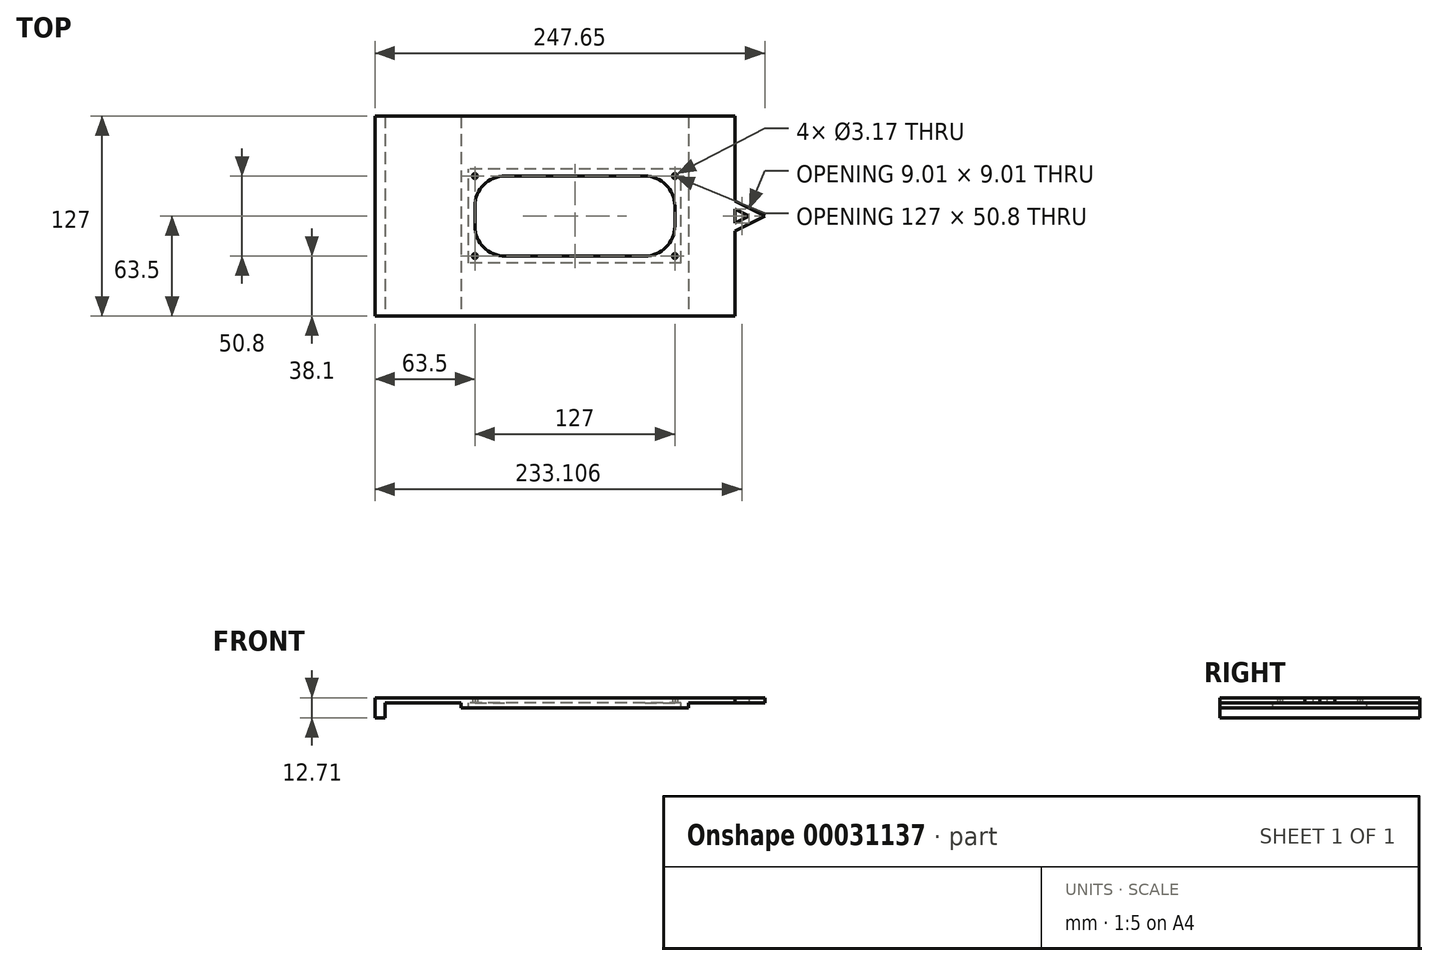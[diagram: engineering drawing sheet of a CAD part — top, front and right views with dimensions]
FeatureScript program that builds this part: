
annotation { "Feature Type Name" : "Feature", "Feature Type Description" : "" }
export const myFeature = defineFeature(function(context is Context, id is Id, definition is map)
    precondition{}
    {
        {
            var Q0;
            Q0=qCreatedBy(makeId("Top.planeOp"),FACE);
            var sketch = newSketch(context, id + "F0", { "sketchPlane" : qUnion([Q0])});
            skLineSegment(sketch, "E0.rect.left", {"start": v(101.6, -63.5) * mm, "end": v(101.6, -9.53) * mm});
            skPoint(sketch, "E0.rect.middle", {"position": v(0, 0) * mm});
            skLineSegment(sketch, "E1.rect.right", {"start": v(-127, -63.5) * mm, "end": v(-127, 63.5) * mm});
            skLineSegment(sketch, "E2.rect.bottom", {"start": v(-127, -63.5) * mm, "end": v(101.6, -63.5) * mm});
            skLineSegment(sketch, "E2.rect.top", {"start": v(-127, 63.5) * mm, "end": v(101.6, 63.5) * mm});
            skLineSegment(sketch, "E3.rect.bottom", {"start": v(44.45, -25.4) * mm, "end": v(-44.45, -25.4) * mm});
            skLineSegment(sketch, "E3.rect.top", {"start": v(44.45, 25.4) * mm, "end": v(-44.45, 25.4) * mm});
            skLineSegment(sketch, "E3.rect.left", {"start": v(63.5, -6.35) * mm, "end": v(63.5, 6.35) * mm});
            skLineSegment(sketch, "E3.rect.right", {"start": v(-63.5, -6.35) * mm, "end": v(-63.5, 6.35) * mm});
            skPoint(sketch, "E4.visualSharp", {"position": v(-63.5, 25.4) * mm});
            skArc(sketch, "E4.filletArc", {"start": v(-44.45, 25.4) * mm, "mid": v(-57.92, 19.82) * mm, "end": v(-63.5, 6.35) * mm});
            skPoint(sketch, "E5.visualSharp", {"position": v(-63.5, -25.4) * mm});
            skArc(sketch, "E5.filletArc", {"start": v(-63.5, -6.35) * mm, "mid": v(-57.92, -19.82) * mm, "end": v(-44.45, -25.4) * mm});
            skPoint(sketch, "E6.visualSharp", {"position": v(63.5, -25.4) * mm});
            skArc(sketch, "E6.filletArc", {"start": v(44.45, -25.4) * mm, "mid": v(57.92, -19.82) * mm, "end": v(63.5, -6.35) * mm});
            skPoint(sketch, "E7.visualSharp", {"position": v(63.5, 25.4) * mm});
            skArc(sketch, "E7.filletArc", {"start": v(63.5, 6.35) * mm, "mid": v(57.92, 19.82) * mm, "end": v(44.45, 25.4) * mm});
            skPoint(sketch, "E8.orphan", {"position": v(-127, 92.44) * mm});
            skPoint(sketch, "E0.rect.top.end.orphan", {"position": v(-101.6, 76.2) * mm});
            skPoint(sketch, "E9.orphan", {"position": v(101.6, 76.2) * mm});
            skPoint(sketch, "E10.orphan", {"position": v(127, 92.44) * mm});
            skPoint(sketch, "E11.orphan", {"position": v(133.35, 63.5) * mm});
            skPoint(sketch, "E12.trimOffspring.end.orphan", {"position": v(133.35, -63.5) * mm});
            skPoint(sketch, "E1.rect.bottom.start.orphan", {"position": v(127, -92.44) * mm});
            skPoint(sketch, "E13.orphan", {"position": v(-101.6, -76.2) * mm});
            skPoint(sketch, "E14.orphan", {"position": v(101.6, -76.2) * mm});
            skPoint(sketch, "E15.orphan", {"position": v(-127, -92.44) * mm});
            skCircle(sketch, "E16", {"center": v(-63.5, -25.4) * mm, "radius": 1.59 * mm});
            skCircle(sketch, "E17", {"center": v(-63.5, 25.4) * mm, "radius": 1.59 * mm});
            skCircle(sketch, "E18", {"center": v(63.5, 25.4) * mm, "radius": 1.59 * mm});
            skCircle(sketch, "E19", {"center": v(63.5, -25.4) * mm, "radius": 1.59 * mm});
            skLineSegment(sketch, "E20.rect.bottom", {"start": v(67.52, -29.8) * mm, "end": v(-67.52, -29.8) * mm});
            skLineSegment(sketch, "E20.rect.top", {"start": v(67.52, 29.8) * mm, "end": v(-67.52, 29.8) * mm});
            skLineSegment(sketch, "E20.rect.left", {"start": v(67.52, -29.8) * mm, "end": v(67.52, 29.8) * mm});
            skLineSegment(sketch, "E20.rect.right", {"start": v(-67.52, -29.8) * mm, "end": v(-67.52, 29.8) * mm});
            skLineSegment(sketch, "E21", {"start": v(-72.28, 34.56) * mm, "end": v(72.28, 34.56) * mm});
            skLineSegment(sketch, "E22", {"start": v(72.28, 34.56) * mm, "end": v(72.28, -34.56) * mm});
            skLineSegment(sketch, "E23", {"start": v(72.28, -34.56) * mm, "end": v(-72.28, -34.56) * mm});
            skLineSegment(sketch, "E24", {"start": v(-72.28, -34.56) * mm, "end": v(-72.28, 34.56) * mm});
            skLineSegment(sketch, "E25", {"start": v(-72.28, -34.56) * mm, "end": v(-72.28, -63.5) * mm});
            skLineSegment(sketch, "E26", {"start": v(72.28, -34.56) * mm, "end": v(72.28, -63.5) * mm});
            skLineSegment(sketch, "E27", {"start": v(-72.28, 34.56) * mm, "end": v(-72.28, 63.5) * mm});
            skLineSegment(sketch, "E28", {"start": v(72.28, 34.56) * mm, "end": v(72.28, 63.5) * mm});
            skPoint(sketch, "E29", {"position": v(101.6, 0) * mm});
            skLineSegment(sketch, "E30", {"start": v(120.65, 0) * mm, "end": v(101.6, 9.53) * mm});
            skLineSegment(sketch, "E31", {"start": v(120.65, 0) * mm, "end": v(101.6, -9.52) * mm});
            skLineSegment(sketch, "E32", {"start": v(101.6, -4.5) * mm, "end": v(110.61, 0) * mm});
            skLineSegment(sketch, "E33", {"start": v(110.61, 0) * mm, "end": v(101.6, 4.5) * mm});
            skLineSegment(sketch, "E34.trimOffspring", {"start": v(101.6, 9.52) * mm, "end": v(101.6, 63.5) * mm});
            skLineSegment(sketch, "E35.trimOffspring", {"start": v(101.6, -4.5) * mm, "end": v(101.6, 4.5) * mm});
            skLineSegment(sketch, "E36", {"start": v(-120.65, 63.5) * mm, "end": v(-120.65, -63.5) * mm});
            skPoint(sketch, "E2.rect.left.end.orphan", {"position": v(-133.35, 63.5) * mm});
            skPoint(sketch, "E37.orphan", {"position": v(-133.35, -63.5) * mm});
            skSolve(sketch);
        }
        {
            var Q0;
            Q0=makeQuery(id+"F0.imprint","IMPRINT",FACE,{"disambiguationData":[TD([[makeQuery(id+"F0.imprint","IMPRINT",EDGE,{"derivedFrom":sQuery(id+"F0.wireOp",EDGE,"E23")}),1.0]])]});
            var Q1;
            Q1=makeQuery(id+"F0.imprint","IMPRINT",FACE,{"disambiguationData":[TD([[makeQuery(id+"F0.imprint","IMPRINT",EDGE,{"derivedFrom":sQuery(id+"F0.wireOp",EDGE,"E3.rect.bottom")}),1.0]])]});
            var Q2;
            Q2=makeQuery(id+"F0.imprint","IMPRINT",FACE,{"disambiguationData":[TD([[makeQuery(id+"F0.imprint","IMPRINT",EDGE,{"derivedFrom":sQuery(id+"F0.wireOp",EDGE,"E20.rect.bottom")}),1.0]])]});
            var Q3;
            Q3=makeQuery(id+"F0.imprint","IMPRINT",FACE,{"disambiguationData":[TD([[makeQuery(id+"F0.imprint","IMPRINT",EDGE,{"derivedFrom":sQuery(id+"F0.wireOp",EDGE,"E21")}),1.0]])]});
            var Q4;
            {var subQ3=sQuery(id+"F0.wireOp",EDGE,"E0.rect.left");Q4=makeQuery(id+"F0.imprint","IMPRINT",FACE,{"disambiguationData":[TD([[makeQuery(id+"F0.imprint","IMPRINT",EDGE,{"derivedFrom":subQ3}),1.0]])]});}
            var Q5;
            {var subQ3=sQuery(id+"F0.wireOp",EDGE,"E1.rect.right");Q5=makeQuery(id+"F0.imprint","IMPRINT",FACE,{"disambiguationData":[TD([[makeQuery(id+"F0.imprint","IMPRINT",EDGE,{"derivedFrom":subQ3}),-1.0]])]});}
            var Q6;
            {var subQ2=sQuery(id+"F0.wireOp",EDGE,"E1.rect.right");Q6=makeQuery(id+"F0.imprint","IMPRINT",FACE,{"disambiguationData":[TD([[makeQuery(id+"F0.imprint","IMPRINT",EDGE,{"derivedFrom":subQ2}),1.0]])]});}
            var Q7;
            Q7=makeQuery(id+"F0.imprint","IMPRINT",FACE,{"disambiguationData":[TD([[makeQuery(id+"F0.imprint","IMPRINT",EDGE,{"derivedFrom":sQuery(id+"F0.wireOp",EDGE,"E24")}),1.0]])]});
            extrude(context, id + "F1", {"entities" : qUnion([Q0, Q1, Q2, Q3, Q4, Q5, Q6, Q7]), "depth" : 3.17 * mm});
        }
        {
            var Q0;
            Q0=makeQuery(id+"F0.imprint","IMPRINT",FACE,{"disambiguationData":[TD([[makeQuery(id+"F0.imprint","IMPRINT",EDGE,{"derivedFrom":sQuery(id+"F0.wireOp",EDGE,"E23")}),1.0]])]});
            var Q1;
            Q1=makeQuery(id+"F0.imprint","IMPRINT",FACE,{"disambiguationData":[TD([[makeQuery(id+"F0.imprint","IMPRINT",EDGE,{"derivedFrom":sQuery(id+"F0.wireOp",EDGE,"E20.rect.bottom")}),1.0]])]});
            var Q2;
            Q2=makeQuery(id+"F0.imprint","IMPRINT",FACE,{"disambiguationData":[TD([[makeQuery(id+"F0.imprint","IMPRINT",EDGE,{"derivedFrom":sQuery(id+"F0.wireOp",EDGE,"E21")}),1.0]])]});
            extrude(context, id + "F2", {"entities" : qUnion([Q0, Q1, Q2]), "operationType" : NewBodyOperationType.ADD, "oppositeDirection" : true, "depth" : 3.17 * mm});
        }
        {
            var Q0;
            {var subQ2=sQuery(id+"F0.wireOp",EDGE,"E1.rect.right");Q0=makeQuery(id+"F0.imprint","IMPRINT",FACE,{"disambiguationData":[TD([[makeQuery(id+"F0.imprint","IMPRINT",EDGE,{"derivedFrom":subQ2}),-1.0]])]});}
            extrude(context, id + "F3", {"entities" : qUnion([Q0]), "operationType" : NewBodyOperationType.ADD, "oppositeDirection" : true, "depth" : 9.52 * mm});
        }
    });
